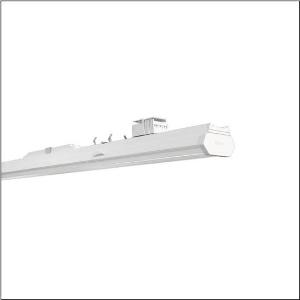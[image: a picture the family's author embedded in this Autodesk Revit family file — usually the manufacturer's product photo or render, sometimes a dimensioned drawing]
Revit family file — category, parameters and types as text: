
# Revit family: licross_r__21_protected_ho_52td12cn4cxm_6843
name_source: partatom
category: Lighting Fixtures
units: mm (PartAtom-declared; Revit-internal decimal feet)

## family parameters
Cut with Voids When Loaded = No
Host = Face
Light Source = No
Part Type = Normal
Room Calculation Point = No
Round Connector Dimension = Use Diameter
Shared = No

## types (1)
- --- (1 x LED, 12460 lm, 68.9 W, 4000K)
    Apparent Load = 69 VA
    CIE Flux Codes = 70 91 97 98 100
    Color Rendering = 80
    Color Temperature = 4000K
    Default Elevation = 1800 mm
    Description = Licross® 21 Protected HO, luminaire insert, of sheet steel, galvanised, coil coated, white, length: 1.500mm, width: 90mm, height: 103mm, LED rated luminous flux: 12.460lm, light colour: 840, SDCM (Standard Deviation of Colour Matching)MacAdam ≤ 3 SDCM (initial), control gear: ON/OFF Multilumen, CLOi, with plug, 3-pole, with phase selection, mains connection: 220..240V, AC, 50/60Hz, start of lifetime: 69W, end of service life: 83W, internal wiring halogen-free, primary light control with lens, of plastic, primary optical cover: cover, of PMMA, light emission: direct distribution, primary light characteristic: symmetric, protection rating (complete): IP54, insulation class (complete): insulation class I (protective earthing), certification: CE, ENEC, VDE, UKCA, protection symbol: D if used in an environment with non-conductive dust loads with corresponding accessories, impact resistance: IK06, permissible ambient temperature for indoor applications: -35..+35°C, corresponds to IFS (International Featured Standards) requirements for safety and quality in the food industry, reducing of maximum allowable ambient temperature of 5°C with ceiling mounting, LABS conformity tested according to VDMA 24364:2018-05, packaging unit: 1 piece
    Height = 92 mm
    Lamp = 1 x LED
    Lamp Light Flux = 12460 lm
    Lamp Power = 68.9 W
    Lamp count = 1
    Length = 1500 mm
    Luminous efficacy = 181 lm/W
    Manufacturer = Siteco
    ModVariant = No
    Model = 52TD12CN4CXM
    Mounting Place = Ceiling
    Mounting Type = Pendant
    Number of Poles = 1
    OnlyDefault = Yes
    Power Factor = 1
    Product Name = Licross® 21 Protected HO
    Product group = luminaire insert | ceiling pendant
    ProductGroupID = 901
    Protection Class = Protection class I
    Protection Degree = IP 54
    RLX_Detail_Level = 1
    RLX_Emergency_Light_Flux = 0 lm
    RLX_Emergency_Type = 0
    RLX_Emergency_Type_DB = No
    RlxData = <blob elided: 22161 chars, md5=3d227c73>
    Socket = socket
    Standby Power = 0 W
    System Light Flux = 12460 lm
    System Power = 69 W
    Type Comments = factory setting: luminous flux: 100 % | (A | C | E) | 162 mA
    Type Image = l_1256148.jpg
    URL = http://relux.com
    VarID = @adj_115407
    Voltage = 0 V
    Weight = 0.00 kg
    Width = 88 mm

## geometry (parser evidence)
native form markers: Blend x4, Sweep x12
no freeform markers — native parametric forms only
